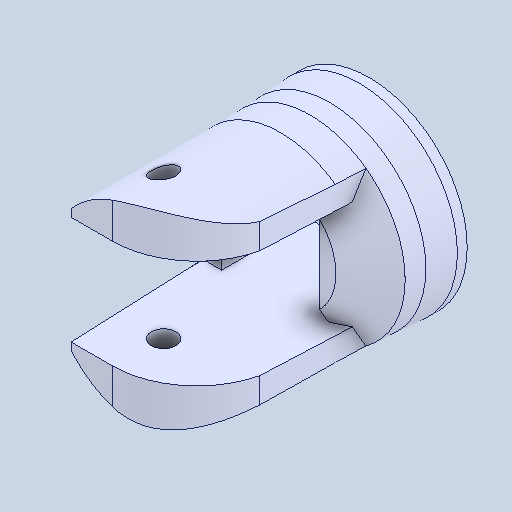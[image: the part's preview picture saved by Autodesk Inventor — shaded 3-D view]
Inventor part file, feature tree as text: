
AUTODESK INVENTOR PART (.ipt)
format: ipt  version: 2022 (Build 260153000, 153)  size: 163,328 bytes
history: mixed  units: mm
features: other x1, chamfer x1, imported_body x1
ambient origin geometry x8: Origin, YZ Plane, XZ Plane, XY Plane, X Axis, Y Axis, Z Axis, Center Point
bodies: Body1 (imported_parasolid)
feature tree (3):
  other  "Sólido1"
  chamfer  "Chamfer1"  [1 undecoded]
  imported_body  NMx_Import_Brep_tag  [imported B-rep: ~8 faces, bbox_mm=[0.0, 7.932497, 0.0]]
note: 1 required parameter value undecoded (feature->parameter linkage not recoverable at this tier; creation-order binding heuristic only, values carry confidence <= 0.55)
